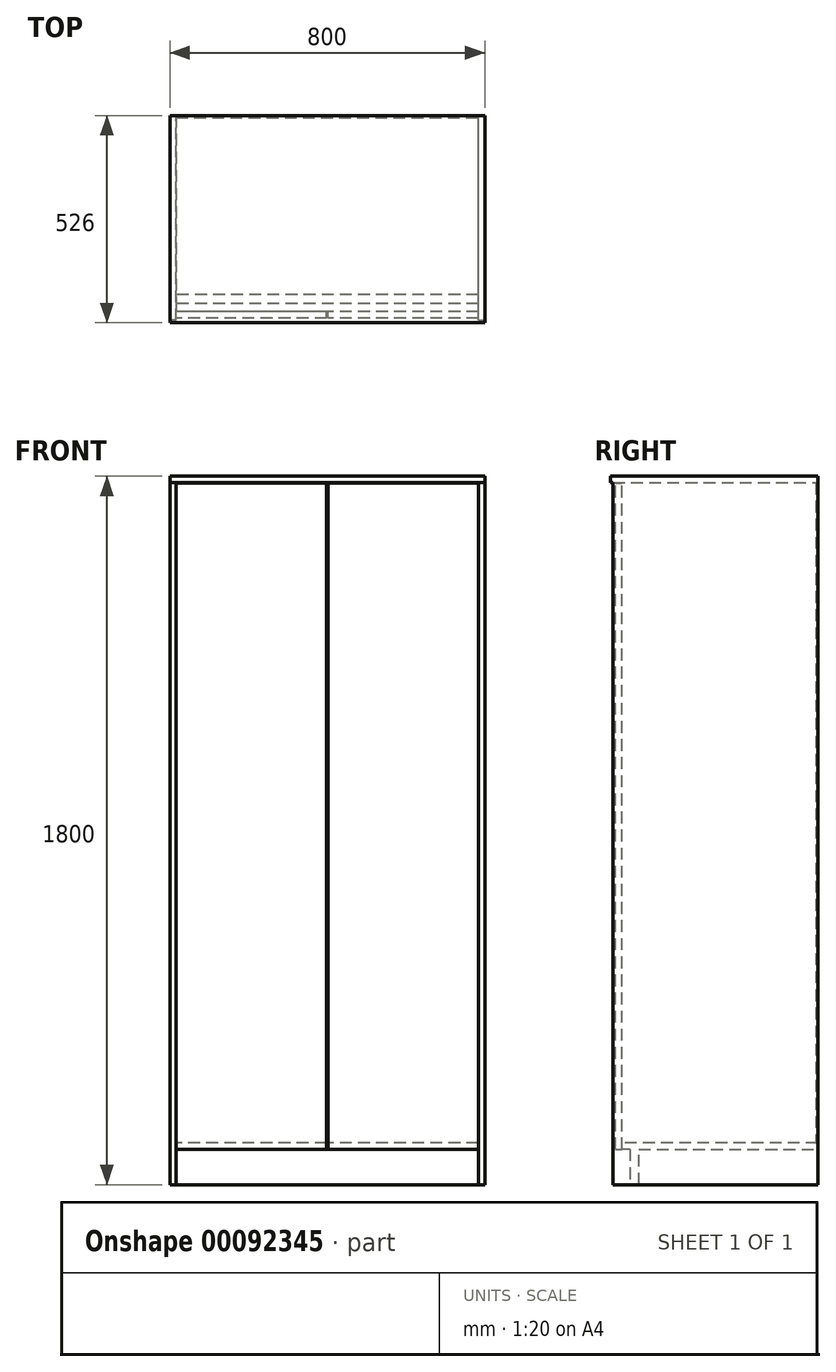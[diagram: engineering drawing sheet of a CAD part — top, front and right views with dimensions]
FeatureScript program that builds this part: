
annotation { "Feature Type Name" : "Feature", "Feature Type Description" : "" }
export const myFeature = defineFeature(function(context is Context, id is Id, definition is map)
    precondition{}
    {
        {
            var Q0;
            Q0=qCreatedBy(makeId("Top.planeOp"),FACE);
            var sketch = newSketch(context, id + "F0", { "sketchPlane" : qUnion([Q0])});
            skLineSegment(sketch, "E0.bottom", {"start": v(-384, 0) * mm, "end": v(-400, 0) * mm});
            skLineSegment(sketch, "E0.top", {"start": v(-384, 520) * mm, "end": v(-400, 520) * mm});
            skLineSegment(sketch, "E0.left", {"start": v(-384, 0) * mm, "end": v(-384, 520) * mm});
            skLineSegment(sketch, "E0.right", {"start": v(-400, 0) * mm, "end": v(-400, 520) * mm});
            skPoint(sketch, "E1.firstSnap0", {"position": v(-392, 0) * mm});
            skLineSegment(sketch, "E1.bottom", {"start": v(384, 0) * mm, "end": v(400, 0) * mm});
            skLineSegment(sketch, "E1.top", {"start": v(384, 520) * mm, "end": v(400, 520) * mm});
            skLineSegment(sketch, "E1.left", {"start": v(384, 0) * mm, "end": v(384, 520) * mm});
            skLineSegment(sketch, "E1.right", {"start": v(400, 0) * mm, "end": v(400, 520) * mm});
            skSolve(sketch);
        }
        {
            var Q0;
            Q0 = qSketchRegion(id + "F0", true);
            extrude(context, id + "F1", {"entities" : qUnion([Q0]), "depth" : 1784 * mm});
        }
        {
            var Q0;
            Q0=makeQuery(id+"F1.opExtrude","CAP_FACE",FACE,{"disambiguationData":[OSD([sQuery(id+"F0.wireOp",EDGE,"E0.bottom"),sQuery(id+"F0.wireOp",EDGE,"E0.top"),sQuery(id+"F0.wireOp",EDGE,"E0.left"),sQuery(id+"F0.wireOp",EDGE,"E0.right")])],"isStart":false});
            var sketch = newSketch(context, id + "F2", { "sketchPlane" : qUnion([Q0])});
            skLineSegment(sketch, "E2.bottom", {"start": v(-400, 520) * mm, "end": v(400, 520) * mm});
            skLineSegment(sketch, "E2.top", {"start": v(-400, -6) * mm, "end": v(400, -6) * mm});
            skLineSegment(sketch, "E2.left", {"start": v(-400, 520) * mm, "end": v(-400, -6) * mm});
            skLineSegment(sketch, "E2.right", {"start": v(400, 520) * mm, "end": v(400, -6) * mm});
            skSolve(sketch);
        }
        {
            var Q0;
            Q0 = qSketchRegion(id + "F2", true);
            extrude(context, id + "F3", {"entities" : qUnion([Q0]), "depth" : 16 * mm});
        }
        {
            var Q0;
            Q0=makeQuery(id+"F1.opExtrude","SWEPT_BODY",BODY,{"disambiguationData":[OSD([sQuery(id+"F0.wireOp",EDGE,"E0.bottom"),sQuery(id+"F0.wireOp",EDGE,"E0.top"),sQuery(id+"F0.wireOp",EDGE,"E0.left"),sQuery(id+"F0.wireOp",EDGE,"E0.right")])]});
            var Q1;
            Q1=makeQuery(id+"F3.opExtrude","SWEPT_BODY",BODY,{"disambiguationData":[OSD([sQuery(id+"F2.wireOp",EDGE,"E2.bottom"),sQuery(id+"F2.wireOp",EDGE,"E2.top"),sQuery(id+"F2.wireOp",EDGE,"E2.left"),sQuery(id+"F2.wireOp",EDGE,"E2.right")])]});
            var Q2;
            Q2=makeQuery(id+"F1.opExtrude","SWEPT_BODY",BODY,{"disambiguationData":[OSD([sQuery(id+"F0.wireOp",EDGE,"E1.bottom"),sQuery(id+"F0.wireOp",EDGE,"E1.top"),sQuery(id+"F0.wireOp",EDGE,"E1.left"),sQuery(id+"F0.wireOp",EDGE,"E1.right")])]});
            booleanBodies(context, id + "F4", {"operationType" : BooleanOperationType.UNION, "tools" : qUnion([Q0, Q1, Q2])});
        }
        {
            var Q0;
            Q0=makeQuery(id+"F1.opExtrude","SWEPT_FACE",FACE,{"disambiguationData":[OSD([sQuery(id+"F0.wireOp",EDGE,"E0.left")])]});
            var sketch = newSketch(context, id + "F5", { "sketchPlane" : qUnion([Q0])});
            skLineSegment(sketch, "E3.bottom", {"start": v(520, 90) * mm, "end": v(65.2, 90) * mm});
            skLineSegment(sketch, "E3.top", {"start": v(520, 106) * mm, "end": v(22, 106) * mm});
            skLineSegment(sketch, "E3.left", {"start": v(520, 90) * mm, "end": v(520, 106) * mm});
            skLineSegment(sketch, "E3.right", {"start": v(22, 90) * mm, "end": v(22, 106) * mm});
            skLineSegment(sketch, "E4.top", {"start": v(42.75, 0) * mm, "end": v(65.2, 0) * mm});
            skLineSegment(sketch, "E4.left", {"start": v(42.75, 90) * mm, "end": v(42.75, 0) * mm});
            skLineSegment(sketch, "E4.right", {"start": v(65.2, 90) * mm, "end": v(65.2, 0) * mm});
            skLineSegment(sketch, "E5.trimOffspring", {"start": v(42.75, 90) * mm, "end": v(22, 90) * mm});
            skSolve(sketch);
        }
        {
            var Q0;
            Q0 = qSketchRegion(id + "F5", true);
            extrude(context, id + "F6", {"entities" : qUnion([Q0]), "operationType" : NewBodyOperationType.ADD, "endBound" : BoundingType.UP_TO_NEXT, "depth" : 25 * mm});
        }
        {
            var Q0;
            Q0=makeQuery(id+"F6.boolean.opBoolean","MERGE",FACE,{"derivedFrom":[makeQuery(id+"F4.opBoolean","MERGE",FACE,{"derivedFrom":[makeQuery(id+"F1.opExtrude","SWEPT_FACE",FACE,{"disambiguationData":[OSD([sQuery(id+"F0.wireOp",EDGE,"E0.top")])]}),makeQuery(id+"F1.opExtrude","SWEPT_FACE",FACE,{"disambiguationData":[OSD([sQuery(id+"F0.wireOp",EDGE,"E1.top")])]}),makeQuery(id+"F3.opExtrude","SWEPT_FACE",FACE,{"disambiguationData":[OSD([sQuery(id+"F2.wireOp",EDGE,"E2.bottom")])]})]}),makeQuery(id+"F6.opExtrude","SWEPT_FACE",FACE,{"disambiguationData":[OSD([sQuery(id+"F5.wireOp",EDGE,"E3.left")])]})]});
            var sketch = newSketch(context, id + "F7", { "sketchPlane" : qUnion([Q0])});
            skLineSegment(sketch, "E6.bottom", {"start": v(-384, 106) * mm, "end": v(384, 106) * mm});
            skLineSegment(sketch, "E6.top", {"start": v(-384, 1784) * mm, "end": v(384, 1784) * mm});
            skLineSegment(sketch, "E6.left", {"start": v(-384, 106) * mm, "end": v(-384, 1784) * mm});
            skLineSegment(sketch, "E6.right", {"start": v(384, 106) * mm, "end": v(384, 1784) * mm});
            skSolve(sketch);
        }
        {
            var Q0;
            Q0 = qSketchRegion(id + "F7", true);
            extrude(context, id + "F8", {"entities" : qUnion([Q0]), "oppositeDirection" : true, "depth" : 5 * mm});
        }
        {
            var Q0;
            Q0=makeQuery(id+"F6.opExtrude","SWEPT_FACE",FACE,{"disambiguationData":[OSD([sQuery(id+"F5.wireOp",EDGE,"E3.right")])]});
            var sketch = newSketch(context, id + "F9", { "sketchPlane" : qUnion([Q0])});
            skLineSegment(sketch, "E7.bottom", {"start": v(-384, 90) * mm, "end": v(-1.5, 90) * mm});
            skLineSegment(sketch, "E7.top", {"start": v(-384, 1782) * mm, "end": v(-1.5, 1782) * mm});
            skLineSegment(sketch, "E7.left", {"start": v(-384, 90) * mm, "end": v(-384, 1782) * mm});
            skLineSegment(sketch, "E7.right", {"start": v(-1.5, 90) * mm, "end": v(-1.5, 1782) * mm});
            skLineSegment(sketch, "E8.bottom", {"start": v(384, 90) * mm, "end": v(1.5, 90) * mm});
            skLineSegment(sketch, "E8.top", {"start": v(384, 1782) * mm, "end": v(1.5, 1782) * mm});
            skLineSegment(sketch, "E8.left", {"start": v(384, 90) * mm, "end": v(384, 1782) * mm});
            skLineSegment(sketch, "E8.right", {"start": v(1.5, 90) * mm, "end": v(1.5, 1782) * mm});
            skSolve(sketch);
        }
        {
            var Q0;
            Q0 = qSketchRegion(id + "F9", true);
            extrude(context, id + "F10", {"entities" : qUnion([Q0]), "depth" : 16 * mm});
        }
    });
